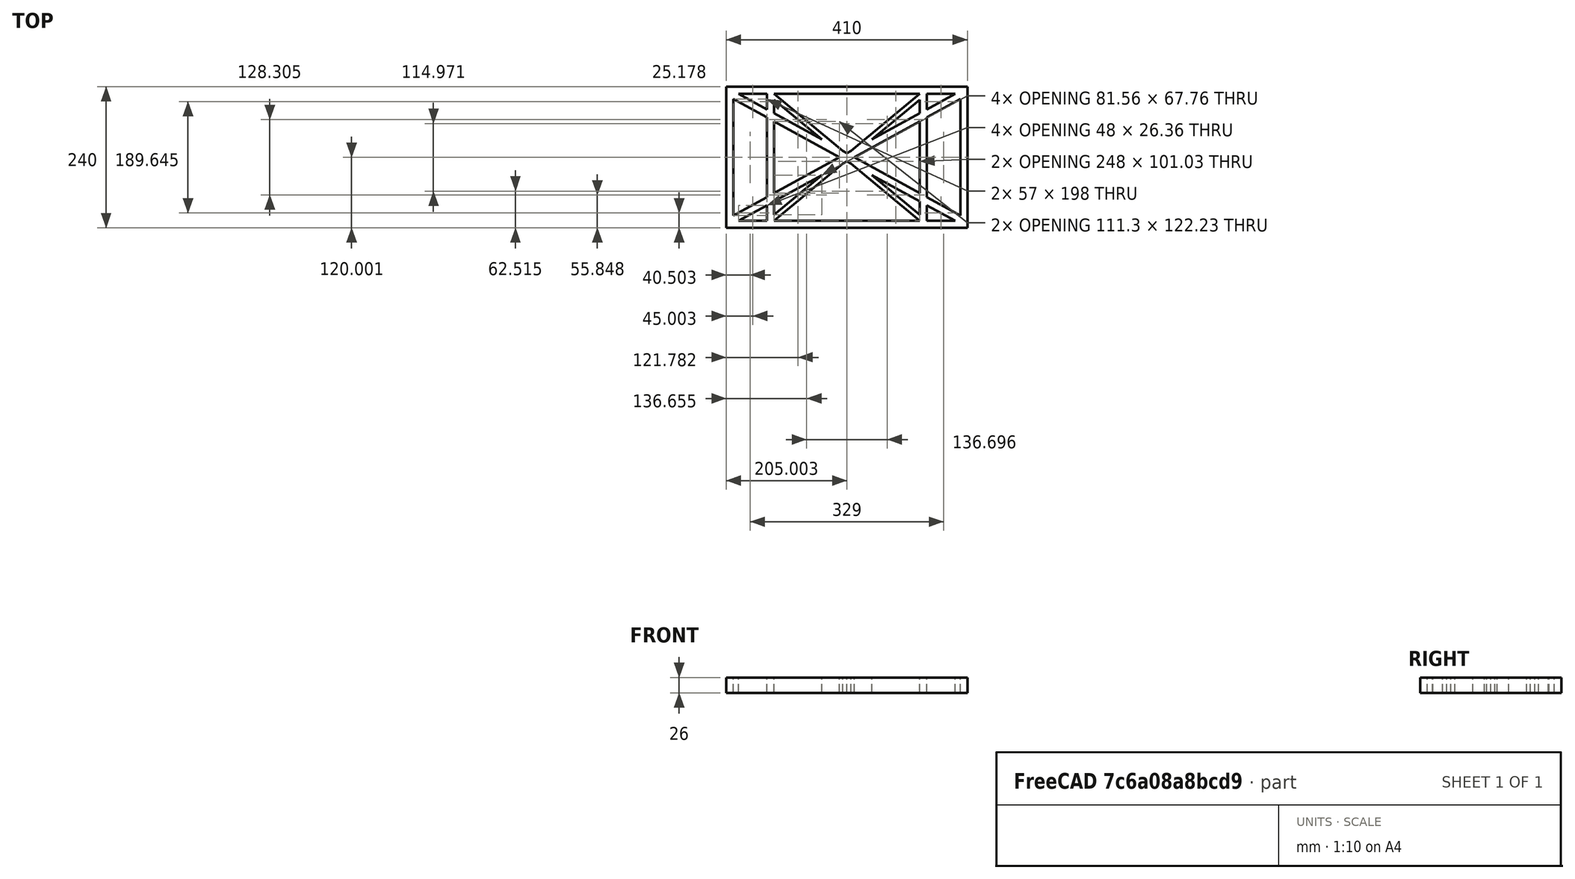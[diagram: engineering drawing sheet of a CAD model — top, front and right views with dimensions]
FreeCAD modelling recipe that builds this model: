
FCSTD DOCUMENT  (FreeCAD 0.19R0.19.2)
Label: laptopStand034
License: All rights reserved
LicenseURL: http://en.wikipedia.org/wiki/All_rights_reserved
objects: Sketcher::SketchObject×3, Part::Extrusion×1
note: 4 computed .brp shape members not serialized (recipe doc carries the construction recipe); baked Part::Feature solids carry a one-line shape summary decoded from their .brp

FEATURE [Sketcher::SketchObject] Sketch
  FullyConstrained = true
  sketch-geometry (52):
    g0: LineSegment StartX=-22.9272 StartY=136.221 StartZ=0 EndX=-22.9272 EndY=-103.779 EndZ=0
    g1: LineSegment StartX=-22.9272 StartY=136.221 StartZ=0 EndX=387.073 EndY=136.221 EndZ=0
    g2: LineSegment StartX=-22.9272 StartY=-103.779 StartZ=0 EndX=387.073 EndY=-103.779 EndZ=0
    g3: LineSegment StartX=387.073 StartY=136.221 StartZ=0 EndX=387.073 EndY=-103.779 EndZ=0
    g4: LineSegment StartX=375.073 StartY=115.221 StartZ=0 EndX=318.073 EndY=83.9235 EndZ=0
    g5: LineSegment StartX=-10.9272 StartY=-82.7794 StartZ=0 EndX=46.0728 EndY=-51.4823 EndZ=0
    g6: LineSegment StartX=-1.92719 StartY=124.221 StartZ=0 EndX=46.0728 EndY=97.8651 EndZ=0
    g7: LineSegment StartX=366.073 StartY=-91.7794 StartZ=0 EndX=318.073 EndY=-65.424 EndZ=0
    g8: LineSegment StartX=-10.9272 StartY=115.221 StartZ=0 EndX=-10.9272 EndY=-82.7794 EndZ=0
    g9: LineSegment StartX=375.073 StartY=-82.7794 StartZ=0 EndX=375.073 EndY=115.221 EndZ=0
    g10: LineSegment StartX=-1.92719 StartY=-91.7794 StartZ=0 EndX=46.0728 EndY=-91.7794 EndZ=0
    g11: LineSegment StartX=318.073 StartY=124.221 StartZ=0 EndX=366.073 EndY=124.221 EndZ=0
    g12: LineSegment StartX=306.073 StartY=-81.8102 StartZ=0 EndX=224.513 EndY=-14.0532 EndZ=0
    g13: LineSegment StartX=58.0728 StartY=114.251 StartZ=0 EndX=139.632 EndY=46.4944 EndZ=0
    g14: LineSegment StartX=306.073 StartY=124.221 StartZ=0 EndX=189.124 EndY=27.0628 EndZ=0
    g15: LineSegment StartX=58.0728 StartY=-91.7794 StartZ=0 EndX=175.022 EndY=5.37834 EndZ=0
    g16: LineSegment StartX=46.0728 StartY=124.221 StartZ=0 EndX=46.0728 EndY=97.8651 EndZ=0
    g17: LineSegment StartX=58.0728 StartY=-81.8102 StartZ=0 EndX=58.0728 EndY=-58.8351 EndZ=0
    g18: LineSegment StartX=318.073 StartY=124.221 StartZ=0 EndX=318.073 EndY=97.8651 EndZ=0
    g19: LineSegment StartX=306.073 StartY=114.251 StartZ=0 EndX=306.073 EndY=91.2763 EndZ=0
    g20: LineSegment StartX=182.073 StartY=23.1914 StartZ=0 EndX=189.124 EndY=27.0628 EndZ=0
    g21: LineSegment StartX=182.073 StartY=9.24976 StartZ=0 EndX=175.022 EndY=5.37834 EndZ=0
    g22: LineSegment StartX=224.513 StartY=46.4944 StartZ=0 EndX=306.073 EndY=114.251 EndZ=0
    g23: LineSegment StartX=175.022 StartY=27.0628 StartZ=0 EndX=58.0728 EndY=124.221 EndZ=0
    g24: LineSegment StartX=169.377 StartY=16.2206 StartZ=0 EndX=58.0728 EndY=77.3346 EndZ=0
    g25: LineSegment StartX=139.632 StartY=-14.0532 StartZ=0 EndX=58.0728 EndY=-81.8102 EndZ=0
    g26: LineSegment StartX=194.768 StartY=16.2206 StartZ=0 EndX=306.073 EndY=-44.8935 EndZ=0
    g27: LineSegment StartX=224.513 StartY=46.4944 StartZ=0 EndX=306.073 EndY=91.2763 EndZ=0
    g28: LineSegment StartX=175.022 StartY=27.0628 StartZ=0 EndX=182.073 EndY=23.1914 EndZ=0
    g29: LineSegment StartX=139.632 StartY=-14.0532 StartZ=0 EndX=58.0728 EndY=-58.8351 EndZ=0
    g30: LineSegment StartX=189.124 StartY=5.37834 StartZ=0 EndX=182.073 EndY=9.24976 EndZ=0
    g31: LineSegment StartX=189.124 StartY=5.37834 StartZ=0 EndX=306.073 EndY=-91.7794 EndZ=0
    g32: LineSegment StartX=306.073 StartY=77.3346 StartZ=0 EndX=306.073 EndY=-44.8935 EndZ=0
    g33: LineSegment StartX=318.073 StartY=83.9235 StartZ=0 EndX=318.073 EndY=-51.4823 EndZ=0
    g34: LineSegment StartX=318.073 StartY=97.8651 StartZ=0 EndX=366.073 EndY=124.221 EndZ=0
    g35: LineSegment StartX=306.073 StartY=77.3346 StartZ=0 EndX=194.768 EndY=16.2206 EndZ=0
    g36: LineSegment StartX=306.073 StartY=-58.8351 StartZ=0 EndX=224.513 EndY=-14.0532 EndZ=0
    g37: LineSegment StartX=306.073 StartY=-58.8351 StartZ=0 EndX=306.073 EndY=-81.8102 EndZ=0
    g38: LineSegment StartX=318.073 StartY=-51.4823 StartZ=0 EndX=375.073 EndY=-82.7794 EndZ=0
    g39: LineSegment StartX=318.073 StartY=-65.424 StartZ=0 EndX=318.073 EndY=-91.7794 EndZ=0
    g40: LineSegment StartX=306.073 StartY=124.221 StartZ=0 EndX=58.0728 EndY=124.221 EndZ=0
    g41: LineSegment StartX=318.073 StartY=-91.7794 StartZ=0 EndX=366.073 EndY=-91.7794 EndZ=0
    g42: LineSegment StartX=58.0728 StartY=-91.7794 StartZ=0 EndX=306.073 EndY=-91.7794 EndZ=0
    g43: LineSegment StartX=58.0728 StartY=-44.8935 StartZ=0 EndX=58.0728 EndY=77.3346 EndZ=0
    g44: LineSegment StartX=46.0728 StartY=-65.424 StartZ=0 EndX=-1.92719 EndY=-91.7794 EndZ=0
    g45: LineSegment StartX=46.0728 StartY=-65.424 StartZ=0 EndX=46.0728 EndY=-91.7794 EndZ=0
    g46: LineSegment StartX=58.0728 StartY=-44.8935 StartZ=0 EndX=169.377 EndY=16.2206 EndZ=0
    g47: LineSegment StartX=58.0728 StartY=91.2763 StartZ=0 EndX=58.0728 EndY=114.251 EndZ=0
    g48: LineSegment StartX=46.0728 StartY=83.9235 StartZ=0 EndX=46.0728 EndY=-51.4823 EndZ=0
    g49: LineSegment StartX=46.0728 StartY=124.221 StartZ=0 EndX=-1.92719 EndY=124.221 EndZ=0
    g50: LineSegment StartX=58.0728 StartY=91.2763 StartZ=0 EndX=139.632 EndY=46.4944 EndZ=0
    g51: LineSegment StartX=46.0728 StartY=83.9235 StartZ=0 EndX=-10.9272 EndY=115.221 EndZ=0
  constraints (102):
    c: Vertical(g0)
    c: Distance(g0) = 240
    c: Horizontal(g1)
    c: Distance(g1) = 410
    c: Coincident(g1,g0)
    c: Coincident(g2,g0)
    c: Horizontal(g2)
    c: Coincident(g3,g1)
    c: Vertical(g3)
    c: Coincident(g2,g3)
    c: Block(g1)
    c: Horizontal(g10)
    c: Horizontal(g11)
    c: PointOnObject(g35,g6)
    c: Coincident(g28,g20)
    c: Coincident(g30,g21)
    c: Tangent(g7,g24)
    c: PointOnObject(g24,g5)
    c: PointOnObject(g26,g4)
    c: Coincident(g20,g14)
    c: Tangent(g20,g27)
    c: Coincident(g50,g13)
    c: Coincident(g28,g23)
    c: Coincident(g22,g27)
    c: Coincident(g21,g15)
    c: Coincident(g29,g25)
    c: Tangent(g21,g29)
    c: Coincident(g36,g12)
    c: Coincident(g31,g30)
    c: Coincident(g22,g19)
    c: Tangent(g19,g32)
    c: Tangent(g18,g33)
    c: Coincident(g27,g19)
    c: Tangent(g27,g34)
    c: Coincident(g4,g33)
    c: Coincident(g35,g32)
    c: Tangent(g4,g35)
    c: Coincident(g37,g12)
    c: Tangent(g7,g36)
    c: Tangent(g32,g37)
    c: Coincident(g26,g32)
    c: Tangent(g26,g38)
    c: Coincident(g33,g38)
    c: Coincident(g39,g7)
    c: Tangent(g33,g39)
    c: Coincident(g25,g17)
    c: Tangent(g17,g43)
    c: Coincident(g29,g17)
    c: Tangent(g29,g44)
    c: Coincident(g45,g44)
    c: Tangent(g16,g45)
    c: Coincident(g5,g48)
    c: Coincident(g46,g43)
    c: Tangent(g5,g46)
    c: Tangent(g43,g47)
    c: Tangent(g16,g48)
    c: Coincident(g13,g47)
    c: PointOnObject(g40,g23)
    c: Tangent(g40,g49)
    c: Coincident(g6,g16)
    c: Coincident(g50,g47)
    c: Tangent(g6,g50)
    c: Coincident(g24,g43)
    c: Coincident(g51,g48)
    c: Tangent(g24,g51)
    c: Block(g23)
    c: Block(g14)
    c: Block(g20)
    c: Block(g40)
    c: Block(g18)
    c: Block(g34)
    c: Block(g4)
    c: Block(g38)
    c: Block(g9)
    c: Block(g36)
    c: Block(g37)
    c: Block(g7)
    c: Block(g39)
    c: Block(g22)
    c: Block(g31)
    c: Block(g42)
    c: Block(g21)
    c: Block(g15)
    c: Block(g29)
    c: Block(g25)
    c: Block(g45)
    c: Block(g44)
    c: Block(g5)
    c: Block(g8)
    c: Block(g51)
    c: Block(g6)
    c: Block(g16)
    c: Block(g13)
    c: Block(g47)
    c: Block(g35)
    c: Block(g32)
    c: Block(g24)
    c: Block(g46)
    c: Block(g49)
    c: Block(g11)
    c: Block(g41)
    c: Block(g10)
FEATURE [Part::Extrusion] Extrude
  Base = -> Sketch
  Dir = (0,0,1)
  DirMode = 2
  FaceMakerClass = Part::FaceMakerBullseye
  LengthFwd = 26
  LengthRev = 0
  Solid = true
  Symmetric = false
FEATURE [Sketcher::SketchObject] Sketch001
  FullyConstrained = true
  MapMode = 4
  Placement = pos=(0,0,0) rot=(0.57735,0.57735,0.57735;2.0944rad)
  Support = -> [Sketch]
  sketch-geometry (46):
    g0: LineSegment StartX=17.2232 StartY=-16.0875 StartZ=0 EndX=117.223 EndY=-16.0875 EndZ=0
    g1: LineSegment StartX=17.2232 StartY=-16.0875 StartZ=0 EndX=17.2232 EndY=-19.0875 EndZ=0
    g2: LineSegment StartX=117.223 StartY=-16.0875 StartZ=0 EndX=117.223 EndY=-19.0875 EndZ=0
    g3: BSplineCurve PolesCount=3 KnotsCount=2 Degree=2 IsPeriodic=0
    g4: LineSegment StartX=17.2232 StartY=-19.0875 StartZ=0 EndX=29.8094 EndY=-19.0875 EndZ=0
    g5: ArcOfCircle CenterX=73.122 CenterY=-32.2909 CenterZ=0 NormalX=0 NormalY=0 NormalZ=1 AngleXU=0 Radius=13 StartAngle=5.92268 EndAngle=9.06428
    g6: LineSegment StartX=85.2864 StartY=-36.8765 StartZ=0 EndX=78.9505 EndY=-53.7246 EndZ=0
    g7: LineSegment StartX=60.9577 StartY=-27.7052 StartZ=0 EndX=54.6191 EndY=-44.5532 EndZ=0
    g8: ArcOfCircle CenterX=66.7816 CenterY=-49.1439 CenterZ=0 NormalX=0 NormalY=0 NormalZ=1 AngleXU=0 Radius=13 StartAngle=2.78068 EndAngle=5.92131
    g9: ArcOfCircle CenterX=55.9263 CenterY=-78.1807 CenterZ=0 NormalX=0 NormalY=0 NormalZ=1 AngleXU=0 Radius=13 StartAngle=5.92268 EndAngle=9.06428
    g10: LineSegment StartX=68.0907 StartY=-82.7664 StartZ=0 EndX=61.7547 EndY=-99.6148 EndZ=0
    g11: ArcOfCircle CenterX=49.5884 CenterY=-95.0342 CenterZ=0 NormalX=0 NormalY=0 NormalZ=1 AngleXU=0 Radius=13 StartAngle=2.78068 EndAngle=5.92131
    g12: LineSegment StartX=43.7619 StartY=-73.595 StartZ=0 EndX=37.426 EndY=-90.4435 EndZ=0
    g13: ArcOfCircle CenterX=38.7206 CenterY=-124.067 CenterZ=0 NormalX=0 NormalY=0 NormalZ=1 AngleXU=0 Radius=13 StartAngle=5.92268 EndAngle=9.06428
    g14: LineSegment StartX=26.5562 StartY=-119.481 StartZ=0 EndX=20.2251 EndY=-136.329 EndZ=0
    g15: ArcOfCircle CenterX=32.3875 CenterY=-140.92 CenterZ=0 NormalX=0 NormalY=0 NormalZ=1 AngleXU=0 Radius=13 StartAngle=2.78068 EndAngle=5.92131
    g16: LineSegment StartX=50.885 StartY=-128.652 StartZ=0 EndX=44.549 EndY=-145.5 EndZ=0
    g17: ArcOfCircle CenterX=21.4715 CenterY=-169.934 CenterZ=0 NormalX=0 NormalY=0 NormalZ=1 AngleXU=0 Radius=13 StartAngle=5.92268 EndAngle=9.06428
    g18: LineSegment StartX=9.3071 StartY=-165.349 StartZ=0 EndX=2.97115 EndY=-182.197 EndZ=0
    g19: ArcOfCircle CenterX=15.1336 CenterY=-186.787 CenterZ=0 NormalX=0 NormalY=0 NormalZ=1 AngleXU=0 Radius=13 StartAngle=2.78068 EndAngle=5.92131
    g20: LineSegment StartX=33.6358 StartY=-174.52 StartZ=0 EndX=27.2999 EndY=-191.368 EndZ=0
    g21-g24: Circle x4 (B-spline internal-alignment scaffolding for g25; pole/knot coordinates omitted)
    g25: BSplineCurve PolesCount=4 KnotsCount=2 Degree=3 IsPeriodic=0
    g26: GeomPoint X=28.8094 Y=-19.0875 Z=0
    g27: GeomPoint X=47.0443 Y=-50.4712 Z=0
    g28: Circle CenterX=53.5586 CenterY=-23.2695 CenterZ=0 NormalX=0 NormalY=0 NormalZ=1 AngleXU=0 Radius=3.24518
    g29: LineSegment StartX=44.1752 StartY=-217.193 StartZ=0 EndX=43.1192 EndY=-220.001 EndZ=0
    g30: LineSegment StartX=-195.441 StartY=-127.082 StartZ=0 EndX=-196.497 EndY=-129.89 EndZ=0
    g31: LineSegment StartX=-196.497 StartY=-129.89 StartZ=0 EndX=43.1192 EndY=-220.001 EndZ=0
    g32: LineSegment StartX=12.8789 StartY=-141.321 StartZ=0 EndX=47.0443 EndY=-50.4712 EndZ=0
    g33: Circle CenterX=-195.441 CenterY=-127.082 CenterZ=0 NormalX=0 NormalY=0 NormalZ=1 AngleXU=0 Radius=1
    g34: Circle CenterX=-8.24091 CenterY=-197.481 CenterZ=0 NormalX=0 NormalY=0 NormalZ=1 AngleXU=0 Radius=1
    g35: Circle CenterX=12.8789 CenterY=-141.321 CenterZ=0 NormalX=0 NormalY=0 NormalZ=1 AngleXU=0 Radius=1
    g36: BSplineCurve PolesCount=3 KnotsCount=2 Degree=2 IsPeriodic=0
    g37: GeomPoint X=-195.441 Y=-127.082 Z=0
    g38: GeomPoint X=12.8789 Y=-141.321 Z=0
    g39: Circle CenterX=-12.8016 CenterY=-179.036 CenterZ=0 NormalX=0 NormalY=0 NormalZ=1 AngleXU=0 Radius=10.5072
    g40: Circle CenterX=0.933922 CenterY=-166.43 CenterZ=0 NormalX=0 NormalY=0 NormalZ=1 AngleXU=0 Radius=3.26661
    g41: Circle CenterX=-33.5518 CenterY=-176.44 CenterZ=0 NormalX=0 NormalY=0 NormalZ=1 AngleXU=0 Radius=5.64388
    g42: Circle CenterX=-47.2366 CenterY=-173.859 CenterZ=0 NormalX=0 NormalY=0 NormalZ=1 AngleXU=0 Radius=3.01653
    g43: Circle CenterX=-56.2595 CenterY=-171.456 CenterZ=0 NormalX=0 NormalY=0 NormalZ=1 AngleXU=0 Radius=2.12826
    g44: ArcOfCircle CenterX=51.2151 CenterY=-198.473 CenterZ=0 NormalX=0 NormalY=0 NormalZ=1 AngleXU=0 Radius=20 StartAngle=2.78189 EndAngle=4.35269
    g45: LineSegment StartX=32.4951 StartY=-191.433 StartZ=0 EndX=94.6577 EndY=-26.1351 EndZ=0
  constraints (80):
    c: Horizontal(g0)
    c: Distance(g0) = 100
    c: Block(g0)
    c: Coincident(g1,g0)
    c: Vertical(g1)
    c: Distance(g1) = 3
    c: Coincident(g2,g0)
    c: Vertical(g2)
    c: Distance(g2) = 3
    c: Block(g3)
    c: Coincident(g3,g2)
    c: Coincident(g4,g1)
    c: Horizontal(g4)
    c: Block(g5)
    c: Distance(g6) = 18
    c: Coincident(g6,g5)
    c: Coincident(g7,g5)
    c: Block(g8)
    c: Coincident(g8,g7)
    c: Block(g7)
    c: Coincident(g10,g9)
    c: Coincident(g12,g9)
    c: Block(g11)
    c: Coincident(g11,g12)
    c: Block(g12)
    c: Block(g9)
    c: Block(g10)
    c: Coincident(g16,g13)
    c: Coincident(g14,g13)
    c: Block(g15)
    c: Coincident(g15,g14)
    c: Block(g14)
    c: Block(g13)
    c: Coincident(g20,g17)
    c: Coincident(g18,g17)
    c: Block(g19)
    c: Coincident(g19,g18)
    c: Block(g18)
    c: Block(g17)
    c: Distance(g20) = 18
    c: Block(g20)
    c: Block(g16)
    c: Block(g6)
    c: Weight(g21) = 1
    c: Equal(g21,g22)
    c: Equal(g21,g23)
    c: Equal(g21,g24)
    c: InternalAlignment(g21-g24 -> g25) x4
    c: InternalAlignment(g26,g25)
    c: InternalAlignment(g27,g25)
    c: Block(g28)
    c: Distance(g29) = 3
    c: Distance(g30) = 3
    c: Coincident(g31,g30)
    c: Coincident(g31,g29)
    c: Block(g31)
    c: Block(g30)
    c: Coincident(g32,g25)
    c: Block(g29)
    c: Weight(g33) = 1
    c: Equal(g33,g34)
    c: Equal(g33,g35)
    c: InternalAlignment(g33,g36)
    c: InternalAlignment(g34,g36)
    c: InternalAlignment(g35,g36)
    c: InternalAlignment(g37,g36)
    c: InternalAlignment(g38,g36)
    c: Block(g36)
    c: Block(g32)
    c: Block(g39)
    c: Block(g40)
    c: Block(g41)
    c: Block(g42)
    c: Block(g43)
    c: Coincident(g44,g29)
    c: Block(g44)
    c: Coincident(g45,g44)
    c: Coincident(g45,g3)
    c: Block(g25)
    c: Block(g4)
FEATURE [Sketcher::SketchObject] Sketch002
  FullyConstrained = true
  Placement = pos=(0,0,0) rot=(-1,0,0;4.71239rad)
